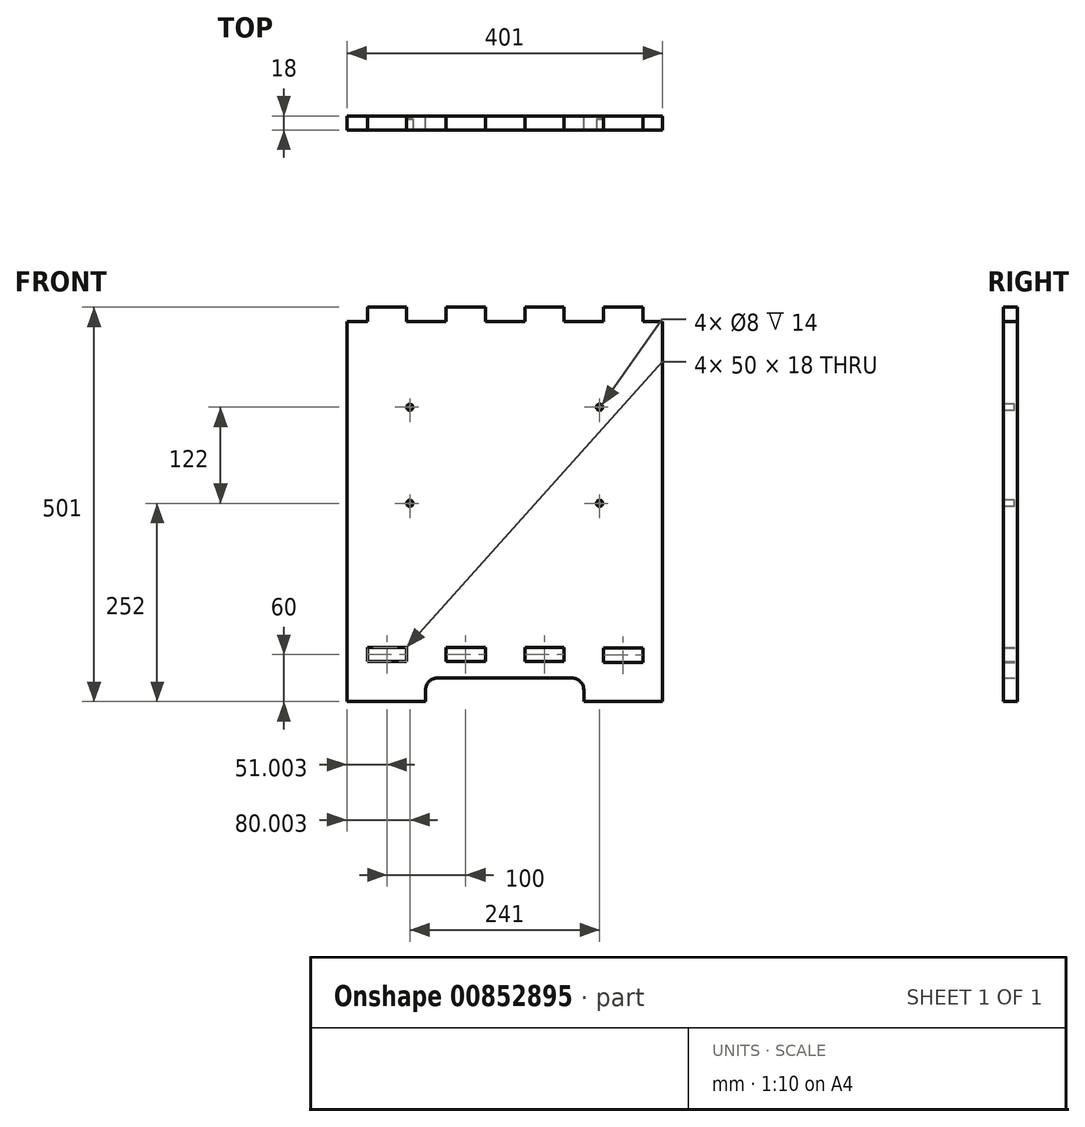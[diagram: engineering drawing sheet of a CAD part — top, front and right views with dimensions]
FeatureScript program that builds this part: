
annotation { "Feature Type Name" : "Feature", "Feature Type Description" : "" }
export const myFeature = defineFeature(function(context is Context, id is Id, definition is map)
    precondition{}
    {
        {
            var Q0;
            Q0=qCreatedBy(makeId("Front.planeOp"),FACE);
            var sketch = newSketch(context, id + "F0", { "sketchPlane" : qUnion([Q0])});
            skLineSegment(sketch, "E0", {"start": v(-164.57, 33) * mm, "end": v(-164.57, 51) * mm});
            skLineSegment(sketch, "E1", {"start": v(-164.57, 51) * mm, "end": v(-114.57, 51) * mm});
            skLineSegment(sketch, "E2", {"start": v(-114.57, 51) * mm, "end": v(-114.57, 33) * mm});
            skLineSegment(sketch, "E3", {"start": v(135.43, 32) * mm, "end": v(135.43, 50) * mm});
            skLineSegment(sketch, "E4", {"start": v(135.43, 50) * mm, "end": v(185.43, 50) * mm});
            skLineSegment(sketch, "E5", {"start": v(185.43, 50) * mm, "end": v(185.43, 32) * mm});
            skLineSegment(sketch, "E6", {"start": v(-164.57, 33) * mm, "end": v(-114.57, 33) * mm});
            skLineSegment(sketch, "E7", {"start": v(135.43, 32) * mm, "end": v(185.43, 32) * mm});
            skLineSegment(sketch, "E8", {"start": v(-90.57, -18) * mm, "end": v(-90.57, -3) * mm});
            skLineSegment(sketch, "E9", {"start": v(-75.57, 12) * mm, "end": v(95.43, 12) * mm});
            skLineSegment(sketch, "E10", {"start": v(110.43, -3) * mm, "end": v(110.43, -18) * mm});
            skPoint(sketch, "E11.visualSharp", {"position": v(-90.57, 12) * mm});
            skArc(sketch, "E11.filletArc", {"start": v(-75.57, 12) * mm, "mid": v(-86.17, 7.6) * mm, "end": v(-90.57, -3) * mm});
            skPoint(sketch, "E12.visualSharp", {"position": v(110.43, 12) * mm});
            skArc(sketch, "E12.filletArc", {"start": v(110.43, -3) * mm, "mid": v(106.04, 7.6) * mm, "end": v(95.43, 12) * mm});
            skLineSegment(sketch, "E13", {"start": v(-190.57, 465) * mm, "end": v(-164.57, 465) * mm});
            skLineSegment(sketch, "E14", {"start": v(-164.57, 465) * mm, "end": v(-164.57, 483) * mm});
            skLineSegment(sketch, "E15", {"start": v(185.43, 483) * mm, "end": v(185.43, 465) * mm});
            skLineSegment(sketch, "E16", {"start": v(185.43, 465) * mm, "end": v(210.43, 465) * mm});
            skLineSegment(sketch, "E17", {"start": v(210.43, 465) * mm, "end": v(210.43, -18) * mm});
            skLineSegment(sketch, "E18", {"start": v(-190.57, 465) * mm, "end": v(-190.57, -18) * mm});
            skLineSegment(sketch, "E19", {"start": v(-190.57, -18) * mm, "end": v(-90.57, -18) * mm});
            skLineSegment(sketch, "E20", {"start": v(110.43, -18) * mm, "end": v(210.43, -18) * mm});
            skLineSegment(sketch, "E21", {"start": v(-164.57, 483) * mm, "end": v(-114.57, 483) * mm});
            skLineSegment(sketch, "E22", {"start": v(-114.57, 483) * mm, "end": v(-114.57, 465) * mm});
            skLineSegment(sketch, "E23", {"start": v(-114.57, 465) * mm, "end": v(-64.57, 465) * mm});
            skLineSegment(sketch, "E24", {"start": v(-64.57, 465) * mm, "end": v(-64.57, 483) * mm});
            skLineSegment(sketch, "E25", {"start": v(-64.57, 483) * mm, "end": v(-14.57, 483) * mm});
            skLineSegment(sketch, "E26", {"start": v(-14.57, 483) * mm, "end": v(-14.57, 465) * mm});
            skLineSegment(sketch, "E27", {"start": v(-14.57, 465) * mm, "end": v(35.43, 465) * mm});
            skLineSegment(sketch, "E28", {"start": v(35.43, 465) * mm, "end": v(35.43, 483) * mm});
            skLineSegment(sketch, "E29", {"start": v(35.43, 483) * mm, "end": v(85.43, 483) * mm});
            skLineSegment(sketch, "E30", {"start": v(85.43, 483) * mm, "end": v(85.43, 465) * mm});
            skLineSegment(sketch, "E31", {"start": v(85.43, 465) * mm, "end": v(135.43, 465) * mm});
            skLineSegment(sketch, "E32", {"start": v(135.43, 465) * mm, "end": v(135.43, 483) * mm});
            skLineSegment(sketch, "E33", {"start": v(135.43, 483) * mm, "end": v(185.43, 483) * mm});
            skLineSegment(sketch, "E34.bottom", {"start": v(-64.57, 51) * mm, "end": v(-14.57, 51) * mm});
            skLineSegment(sketch, "E34.top", {"start": v(-64.57, 33) * mm, "end": v(-14.57, 33) * mm});
            skLineSegment(sketch, "E34.left", {"start": v(-64.57, 51) * mm, "end": v(-64.57, 33) * mm});
            skLineSegment(sketch, "E34.right", {"start": v(-14.57, 51) * mm, "end": v(-14.57, 33) * mm});
            skLineSegment(sketch, "E35.bottom", {"start": v(35.43, 51) * mm, "end": v(85.43, 51) * mm});
            skLineSegment(sketch, "E35.top", {"start": v(35.43, 33) * mm, "end": v(85.43, 33) * mm});
            skLineSegment(sketch, "E35.left", {"start": v(35.43, 51) * mm, "end": v(35.43, 33) * mm});
            skLineSegment(sketch, "E35.right", {"start": v(85.43, 51) * mm, "end": v(85.43, 33) * mm});
            skSolve(sketch);
        }
        {
            var Q0;
            Q0=makeQuery(id+"F0.imprint","IMPRINT",FACE,{"disambiguationData":[TD([[makeQuery(id+"F0.imprint","IMPRINT",EDGE,{"derivedFrom":sQuery(id+"F0.wireOp",EDGE,"E0")}),1.0]])]});
            extrude(context, id + "F1", {"entities" : qUnion([Q0]), "depth" : 18 * mm, "offsetDistance" : 25 * mm});
        }
        {
            var Q0;
            Q0=makeQuery(id+"F1.opExtrude","CAP_FACE",FACE,{"disambiguationData":[OSD([sQuery(id+"F0.wireOp",EDGE,"E0"),sQuery(id+"F0.wireOp",EDGE,"E1"),sQuery(id+"F0.wireOp",EDGE,"E2"),sQuery(id+"F0.wireOp",EDGE,"E3"),sQuery(id+"F0.wireOp",EDGE,"E4"),sQuery(id+"F0.wireOp",EDGE,"E5"),sQuery(id+"F0.wireOp",EDGE,"E6"),sQuery(id+"F0.wireOp",EDGE,"E7"),sQuery(id+"F0.wireOp",EDGE,"E8"),sQuery(id+"F0.wireOp",EDGE,"E9"),sQuery(id+"F0.wireOp",EDGE,"E10"),sQuery(id+"F0.wireOp",EDGE,"E11.filletArc"),sQuery(id+"F0.wireOp",EDGE,"E12.filletArc"),sQuery(id+"F0.wireOp",EDGE,"E13"),sQuery(id+"F0.wireOp",EDGE,"E14"),sQuery(id+"F0.wireOp",EDGE,"E15"),sQuery(id+"F0.wireOp",EDGE,"E16"),sQuery(id+"F0.wireOp",EDGE,"E17"),sQuery(id+"F0.wireOp",EDGE,"E18"),sQuery(id+"F0.wireOp",EDGE,"E19"),sQuery(id+"F0.wireOp",EDGE,"E20"),sQuery(id+"F0.wireOp",EDGE,"E21"),sQuery(id+"F0.wireOp",EDGE,"E22"),sQuery(id+"F0.wireOp",EDGE,"E23"),sQuery(id+"F0.wireOp",EDGE,"E24"),sQuery(id+"F0.wireOp",EDGE,"E25"),sQuery(id+"F0.wireOp",EDGE,"E26"),sQuery(id+"F0.wireOp",EDGE,"E27"),sQuery(id+"F0.wireOp",EDGE,"E28"),sQuery(id+"F0.wireOp",EDGE,"E29"),sQuery(id+"F0.wireOp",EDGE,"E30"),sQuery(id+"F0.wireOp",EDGE,"E31"),sQuery(id+"F0.wireOp",EDGE,"E32"),sQuery(id+"F0.wireOp",EDGE,"E33"),sQuery(id+"F0.wireOp",EDGE,"E34.bottom"),sQuery(id+"F0.wireOp",EDGE,"E34.top"),sQuery(id+"F0.wireOp",EDGE,"E34.left"),sQuery(id+"F0.wireOp",EDGE,"E34.right"),sQuery(id+"F0.wireOp",EDGE,"E35.bottom"),sQuery(id+"F0.wireOp",EDGE,"E35.top"),sQuery(id+"F0.wireOp",EDGE,"E35.left"),sQuery(id+"F0.wireOp",EDGE,"E35.right")])],"isStart":false});
            var sketch = newSketch(context, id + "F2", { "sketchPlane" : qUnion([Q0])});
            skCircle(sketch, "E36", {"center": v(130.43, 234) * mm, "radius": 4 * mm});
            skCircle(sketch, "E37", {"center": v(-110.57, 234) * mm, "radius": 4 * mm});
            skCircle(sketch, "E38", {"center": v(130.43, 356) * mm, "radius": 4 * mm});
            skCircle(sketch, "E39", {"center": v(-110.57, 356) * mm, "radius": 4 * mm});
            skSolve(sketch);
        }
        {
            var Q0;
            Q0=makeQuery(id+"F2.imprint","IMPRINT",FACE,{"disambiguationData":[TD([[makeQuery(id+"F2.imprint","IMPRINT",EDGE,{"derivedFrom":sQuery(id+"F2.wireOp",EDGE,"E36")}),1.0]])]});
            var Q1;
            Q1=makeQuery(id+"F2.imprint","IMPRINT",FACE,{"disambiguationData":[TD([[makeQuery(id+"F2.imprint","IMPRINT",EDGE,{"derivedFrom":sQuery(id+"F2.wireOp",EDGE,"E39")}),1.0]])]});
            var Q2;
            Q2=makeQuery(id+"F2.imprint","IMPRINT",FACE,{"disambiguationData":[TD([[makeQuery(id+"F2.imprint","IMPRINT",EDGE,{"derivedFrom":sQuery(id+"F2.wireOp",EDGE,"E37")}),1.0]])]});
            var Q3;
            Q3=makeQuery(id+"F2.imprint","IMPRINT",FACE,{"disambiguationData":[TD([[makeQuery(id+"F2.imprint","IMPRINT",EDGE,{"derivedFrom":sQuery(id+"F2.wireOp",EDGE,"E38")}),1.0]])]});
            extrude(context, id + "F3", {"entities" : qUnion([Q0, Q1, Q2, Q3]), "operationType" : NewBodyOperationType.REMOVE, "oppositeDirection" : true, "depth" : 14 * mm, "offsetDistance" : 25 * mm});
        }
    });
